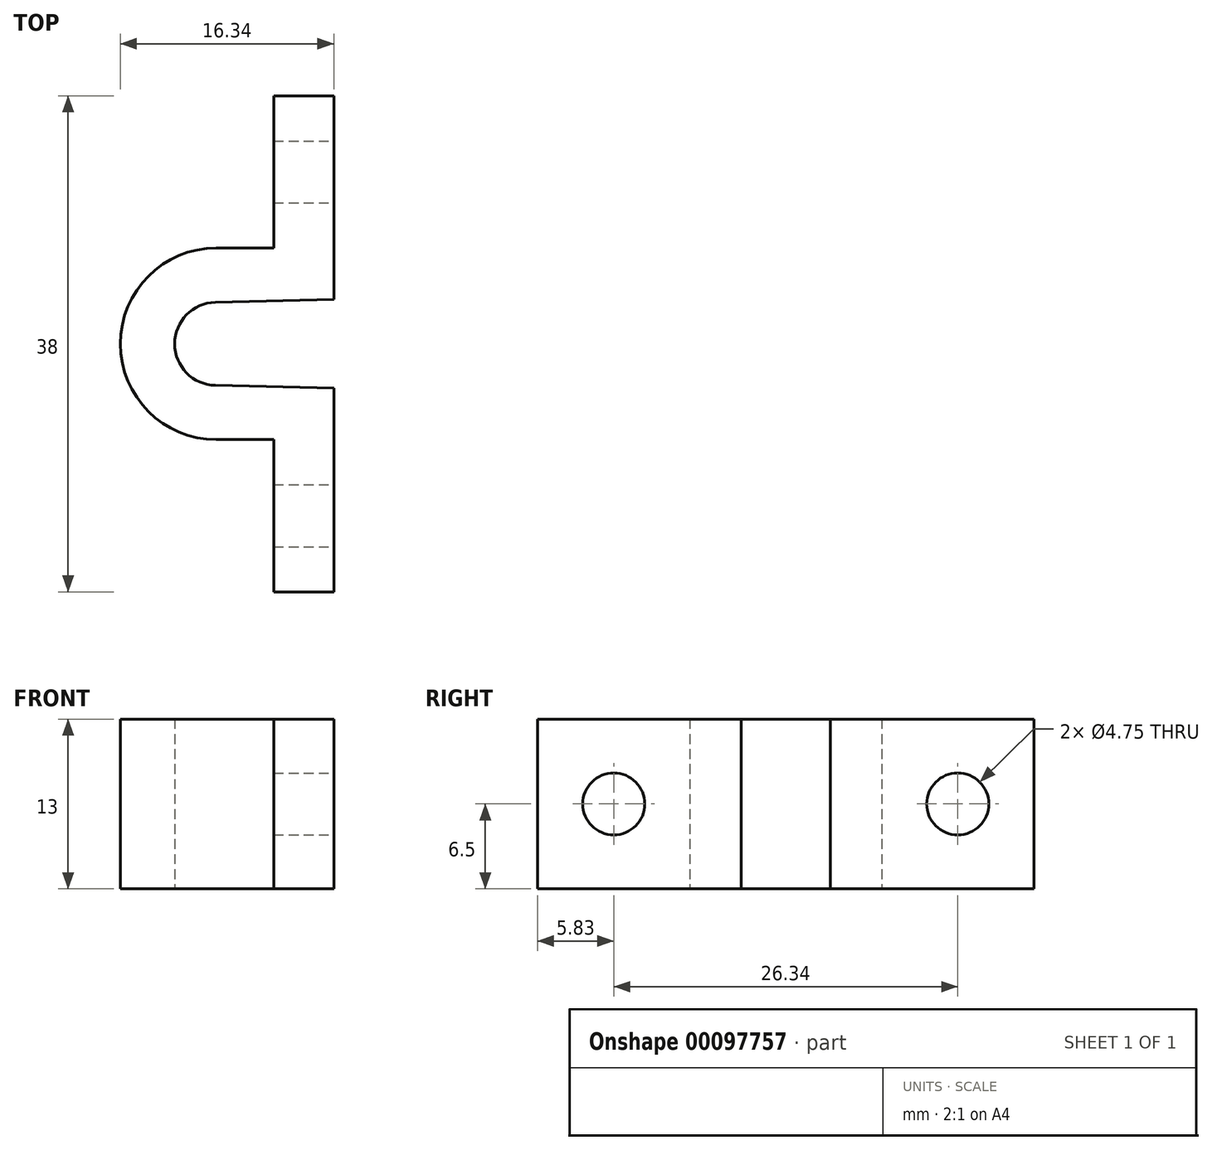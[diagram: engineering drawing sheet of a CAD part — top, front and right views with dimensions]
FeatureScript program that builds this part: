
annotation { "Feature Type Name" : "Feature", "Feature Type Description" : "" }
export const myFeature = defineFeature(function(context is Context, id is Id, definition is map)
    precondition{}
    {
        {
            var Q0;
            Q0=qCreatedBy(makeId("Top.planeOp"),FACE);
            var sketch = newSketch(context, id + "F0", { "sketchPlane" : qUnion([Q0])});
            skLineSegment(sketch, "E0", {"start": v(0, -19) * mm, "end": v(-4.6, -19) * mm});
            skLineSegment(sketch, "E1", {"start": v(0, 19) * mm, "end": v(-4.6, 19) * mm});
            skLineSegment(sketch, "E2", {"start": v(-4.6, 19) * mm, "end": v(-4.6, 7.34) * mm});
            skLineSegment(sketch, "E3", {"start": v(-4.6, -19) * mm, "end": v(-4.6, -7.34) * mm});
            skLineSegment(sketch, "E4", {"start": v(0, 19) * mm, "end": v(0, 3.4) * mm});
            skLineSegment(sketch, "E5", {"start": v(0, -19) * mm, "end": v(0, -3.4) * mm});
            skPoint(sketch, "E6", {"position": v(-9, 0) * mm});
            skArc(sketch, "E7", {"start": v(-9.08, 3.18) * mm, "mid": v(-12.19, 0) * mm, "end": v(-9.08, -3.18) * mm});
            skLineSegment(sketch, "E8", {"start": v(0, 3.4) * mm, "end": v(-9.08, 3.18) * mm});
            skLineSegment(sketch, "E9", {"start": v(0, -3.4) * mm, "end": v(-9.08, -3.18) * mm});
            skLineSegment(sketch, "E10", {"start": v(-4.6, 7.34) * mm, "end": v(-9, 7.34) * mm});
            skLineSegment(sketch, "E11", {"start": v(-4.6, -7.34) * mm, "end": v(-9, -7.34) * mm});
            skArc(sketch, "E12", {"start": v(-9, 7.34) * mm, "mid": v(-16.34, 0) * mm, "end": v(-9, -7.34) * mm});
            skSolve(sketch);
        }
        {
            var Q0;
            Q0=makeQuery(id+"F0.imprint","IMPRINT",FACE,{"disambiguationData":[TD([[makeQuery(id+"F0.imprint","IMPRINT",EDGE,{"derivedFrom":sQuery(id+"F0.wireOp",EDGE,"E0")}),-1.0]])]});
            extrude(context, id + "F1", {"entities" : qUnion([Q0]), "depth" : 13 * mm});
        }
        {
            var Q0;
            Q0=qCreatedBy(makeId("Right.planeOp"),FACE);
            var sketch = newSketch(context, id + "F2", { "sketchPlane" : qUnion([Q0])});
            skLineSegment(sketch, "E13.0", {"start": v(-19, 13) * mm, "end": v(-19, 0) * mm});
            skLineSegment(sketch, "E14.0", {"start": v(-19, 13) * mm, "end": v(-7.34, 13) * mm});
            skLineSegment(sketch, "E15.0", {"start": v(19, 13) * mm, "end": v(7.34, 13) * mm});
            skLineSegment(sketch, "E16.0", {"start": v(19, 13) * mm, "end": v(19, 0) * mm});
            skLineSegment(sketch, "E17.0", {"start": v(-7.34, 13) * mm, "end": v(-7.34, 0) * mm});
            skLineSegment(sketch, "E18.0", {"start": v(7.34, 13) * mm, "end": v(7.34, 0) * mm});
            skPoint(sketch, "E19.orphan", {"position": v(-3.4, 13) * mm});
            skPoint(sketch, "E20.orphan", {"position": v(3.4, 13) * mm});
            skCircle(sketch, "E21", {"center": v(-13.17, 6.5) * mm, "radius": 2.38 * mm});
            skPoint(sketch, "E21.centerSnap0", {"position": v(-13.17, 13) * mm});
            skPoint(sketch, "E21.centerSnap1", {"position": v(-7.34, 6.5) * mm});
            skCircle(sketch, "E22", {"center": v(13.17, 6.5) * mm, "radius": 2.38 * mm});
            skPoint(sketch, "E22.centerSnap0", {"position": v(7.34, 6.5) * mm});
            skPoint(sketch, "E22.centerSnap1", {"position": v(13.17, 13) * mm});
            skSolve(sketch);
        }
        {
            var Q0;
            Q0 = qSketchRegion(id + "F2", true);
            var Q1;
            Q1=makeQuery(id+"F1.opExtrude","SWEPT_FACE",FACE,{"disambiguationData":[OSD([sQuery(id+"F0.wireOp",EDGE,"E3")])]});
            extrude(context, id + "F3", {"entities" : qUnion([Q0]), "operationType" : NewBodyOperationType.REMOVE, "endBound" : BoundingType.UP_TO_SURFACE, "oppositeDirection" : true, "endBoundEntityFace" : qUnion([Q1]), "depth" : 25 * mm});
        }
    });
